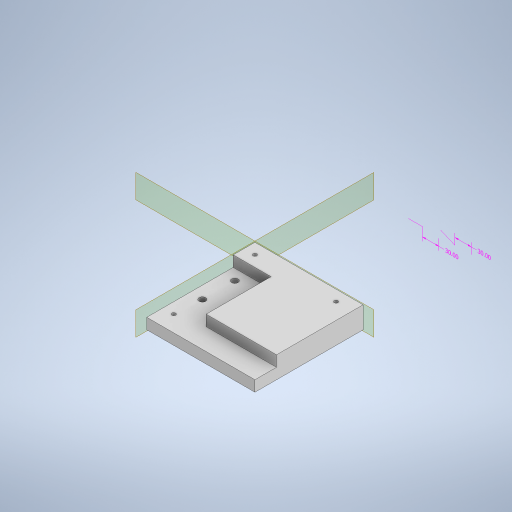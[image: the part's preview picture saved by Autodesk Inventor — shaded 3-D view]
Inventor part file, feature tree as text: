
AUTODESK INVENTOR PART (.ipt)
format: ipt  version: 2023 (Build 270158000, 158)  size: 375,296 bytes
history: native  units: mm
features: sketch x8, extrude x5, other x4, hole x3, plane x2, split x2
ambient origin geometry x8: Origin, YZ Plane, XZ Plane, XY Plane, X Axis, Y Axis, Z Axis, Center Point
bodies: Body1 (feature_tree)
feature tree (24):
  other  "Sólido1"
  other  "Anotaciones"
  extrude  "Extrusión1"  Depth=200.0mm
  extrude  "Extrusión2"  Depth=10.0mm TaperAngle=0.0deg
  extrude  "Extrusión3"  Depth=20.0mm
  hole  "Agujero1"  [1 undecoded]
  extrude  "Extrusión4"  Depth=10.0mm
  plane  "Plano de trabajo1"
  plane  "Plano de trabajo2"
  hole  "Agujero2"  [1 undecoded]
  extrude  "Extrusión5"  Depth=10.0mm TaperAngle=0.0deg
  hole  "Agujero3"  [1 undecoded]
  split  "Dividir3"
  split  "Dividir4"
  sketch  "Boceto1"  dims[d0=200.0mm d1=200.0mm]
  sketch  "Boceto2"  dims[d2=20.0mm d3=0.0mm]
  sketch  "Boceto3"  dims[d4=20.0mm d5=20.0mm d6=30.0mm d7=30.0mm d8=20.0mm d9=35.0mm d10=35.0mm d11=60.0mm d12=10.0mm d13=0.0mm]
  sketch  "Boceto4"  dims[d14=20.0mm d15=0.0mm]
  sketch  "Boceto5"  dims[d16=3.5mm d18=1.75mm d19=1.75mm d20=1.75mm d21=1.75mm d22=10.0mm d23=10.0mm d25=20.0mm]
  sketch  "Boceto7"  dims[d26=40.0mm d27=40.0mm]
  sketch  "Boceto8"  dims[d28=3.5mm d29=6.0mm d30=4.0mm d31=2.0mm d32=90.0deg d33=8.0mm d34=20.594885mm d38=10.0mm]
  sketch  "Boceto9"  dims[d39=10.0mm d40=40.0mm d41=10.0mm d42=0.0mm d52=3.5mm d54=10.0mm d55=10.0mm d56=3.5mm d57=6.0mm d58=4.0mm d59=2.0mm d60=90.0deg d61=8.0mm d62=20.594885mm d63=30.0mm d64=30.0mm d65=10.0mm d66=0.0mm d67=3.5mm d68=15.0mm d69=10.0mm d70=45.0deg d71=45.0deg d72=3.5mm d73=6.0mm d74=4.0mm d75=2.0mm d76=90.0deg d77=8.0mm d78=20.594885mm d43=6.672192mm d44=4.931866mm d45=30.0mm d46=5.890777mm d47=4.508932mm d48=30.0mm d83=0.5mm d84=0.872665mm d85=0.5mm d86=0.872665mm]
  other  "Cota lineal 1"
  other  "Cota lineal 2"
note: 3 required parameter values undecoded (feature->parameter linkage not recoverable at this tier; creation-order binding heuristic only, values carry confidence <= 0.55)
